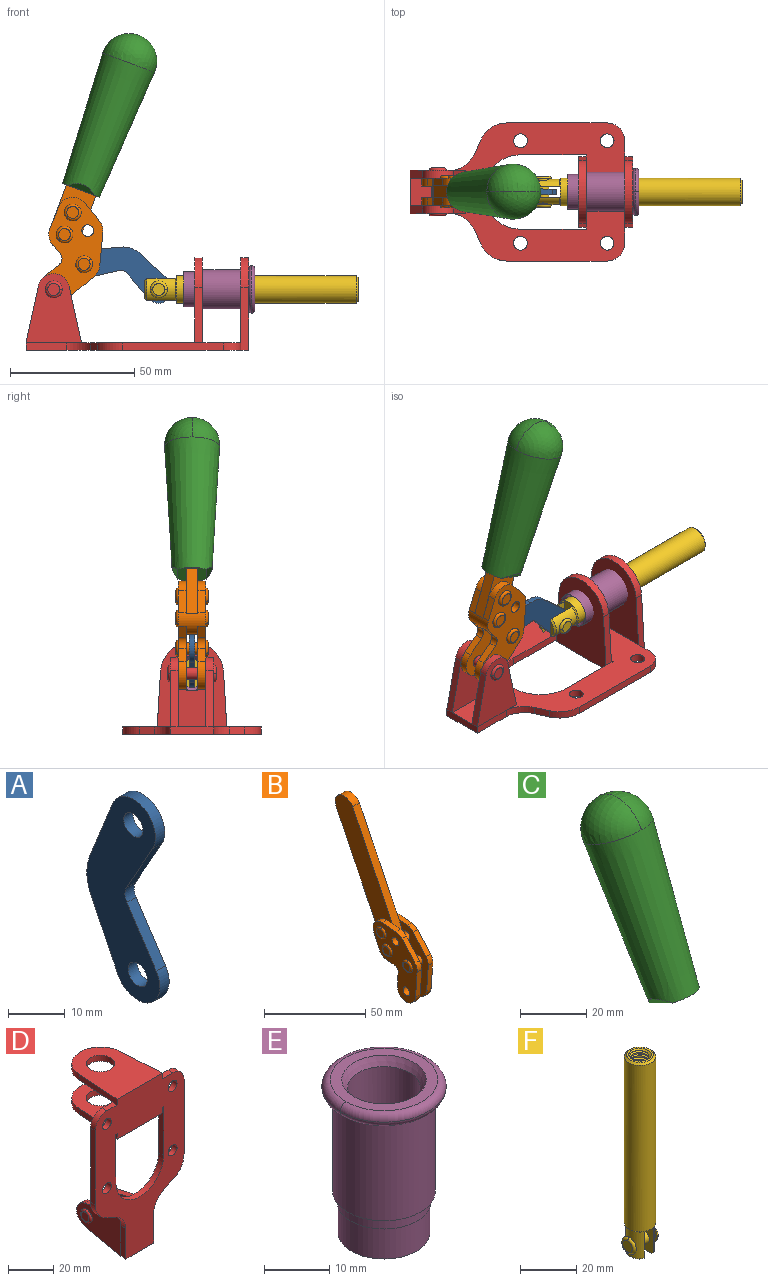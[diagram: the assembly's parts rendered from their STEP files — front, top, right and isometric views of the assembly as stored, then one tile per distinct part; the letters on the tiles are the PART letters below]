
ASSEMBLY  parts=6 mates=6
PART A: 12 faces, bbox 2.3x18.2x42.8 mm
  f0: cylinder r=2.4mm len=4.8mm, axis (1,0,0), area 34.9mm2, adj f4,f11
  f1: cylinder r=10.41mm len=8.47mm, axis (1,0,0), area 20.2mm2, adj f4,f9,f10,f11
  f2: cylinder r=3.05mm len=3.16mm, axis (1,0,0), area 7.7mm2, adj f4,f6,f7,f11
  f3: cylinder r=2.4mm len=4.8mm, axis (1,0,0), area 34.9mm2, adj f4,f11
  f4: plane 42.81x18.23mm, normal (-1,0,0), area 414.1mm2, adj f0,f1,f2,f3,f5,f6,f7,f8
  f5: cylinder r=5.54mm len=10.67mm, axis (1,0,0), area 41.8mm2, adj f4,f6,f10,f11
  f6: plane 11.66x6.53mm, normal (0,-0.87,-0.49), area 30.9mm2, adj f2,f4,f5,f11
  f7: plane 11.17x7.33mm, normal (0,-0.84,0.55), area 30.9mm2, adj f2,f4,f8,f11
  f8: cylinder r=5.54mm len=10.51mm, axis (1,0,0), area 41.8mm2, adj f4,f7,f9,f11
  f9: plane 13.67x6.67mm, normal (0,0.9,-0.44), area 35.1mm2, adj f1,f4,f8,f11
  f10: plane 14.1x5.7mm, normal (0,0.93,0.37), area 35.1mm2, adj f1,f4,f5,f11
  f11: plane 42.81x18.23mm, normal (1,0,0), area 414.1mm2, adj f0,f1,f2,f3,f5,f6,f7,f8
PART B: 59 faces, bbox 12.9x60.2x99.6 mm
  f0: torus R=2.39mm, axis (-1,0,0), area 14.9mm2, adj f20,f43,f51
  f1: torus R=2.39mm, axis (-1,0,0), area 14.9mm2, adj f19,f42,f51
  f2: torus R=2.39mm, axis (-1,0,0), area 14.9mm2, adj f18,f35,f51
  f3: torus R=2.39mm, axis (-1,0,0), area 14.9mm2, adj f14,f17,f23
  f4: torus R=2.39mm, axis (-1,0,0), area 14.9mm2, adj f13,f16,f23
  f5: torus R=2.39mm, axis (-1,0,0), area 14.9mm2, adj f12,f15,f23
  f6: cylinder r=2.39mm len=4.78mm, axis (1,0,0), area 46.5mm2, adj f48,f50,f51
  f7: cylinder r=2.39mm len=4.78mm, axis (1,0,0), area 46.5mm2, adj f50,f51
  f8: cylinder r=6.35mm len=12.68mm, axis (1,0,0), area 61.8mm2, adj f38,f39,f50,f51
  f9: cylinder r=2.39mm len=4.78mm, axis (-1,0,0), area 70.5mm2, adj f46,f50
  f10: cylinder r=2.39mm len=4.78mm, axis (-1,0,0), area 46.5mm2, adj f23,f45,f46
  f11: cylinder r=2.39mm len=4.78mm, axis (-1,0,0), area 46.5mm2, adj f23,f46
  f12: plane 4.78x4.78mm, normal (1,0,0), area 17.9mm2, adj f5,f15
  f13: plane 4.78x4.78mm, normal (1,0,0), area 17.9mm2, adj f4,f16
  f14: plane 4.78x4.78mm, normal (1,0,0), area 17.9mm2, adj f3,f17
  f15: torus R=2.39mm, axis (-1,0,0), area 14.9mm2, adj f5,f12,f23
  f16: torus R=2.39mm, axis (-1,0,0), area 14.9mm2, adj f4,f13,f23
  f17: torus R=2.39mm, axis (-1,0,0), area 14.9mm2, adj f3,f14,f23
  f18: plane 4.78x4.78mm, normal (-1,0,0), area 17.9mm2, adj f2,f35
  f19: plane 4.78x4.78mm, normal (-1,0,0), area 17.9mm2, adj f1,f42
  f20: plane 4.78x4.78mm, normal (-1,0,0), area 17.9mm2, adj f0,f43
  f21: plane 2.26x0.2mm, normal (1,0,0), area 0.2mm2, adj f31,f44
  f22: plane 2.26x0.2mm, normal (-1,0,0), area 0.2mm2, adj f41,f44
  f23: plane 39.37x30.77mm, normal (1,0,0), area 565.5mm2, adj f3,f4,f5,f10,f11,f15,f16,f17
  f24: cylinder r=6.1mm len=4.15mm, axis (-1,0,0), area 14.7mm2, adj f23,f25,f32,f46
  f25: plane 10.25x9.01mm, normal (0,-0.75,0.66), area 42.3mm2, adj f23,f24,f26,f46
  f26: cylinder r=6.35mm len=4.64mm, axis (-1,0,0), area 15.6mm2, adj f23,f25,f27,f46
  f27: plane 15.84x3.1mm, normal (0,-1,-0.07), area 49.2mm2, adj f23,f26,f28,f46
  f28: cylinder r=6.35mm len=12.68mm, axis (-1,0,0), area 61.8mm2, adj f23,f27,f29,f46
  f29: plane 8.11x3.1mm, normal (0,1,0.07), area 25.2mm2, adj f23,f28,f30,f46
  f30: cylinder r=3.05mm len=3.25mm, axis (-1,0,0), area 14.8mm2, adj f23,f29,f31,f46
  f31: plane 5.99x3.1mm, normal (0,0.07,-1), area 18.6mm2, adj f21,f23,f30,f44,f46
  f32: plane 9.5x3.1mm, normal (0,-0.07,1), area 29.5mm2, adj f23,f24,f33,f46,f47
  f33: cylinder r=6.1mm len=8.63mm, axis (-1,0,0), area 39.1mm2, adj f23,f32,f34,f47
  f34: plane 8.65x3.96mm, normal (0,0.91,-0.42), area 29.5mm2, adj f23,f33,f44,f47
  f35: torus R=2.39mm, axis (-1,0,0), area 14.9mm2, adj f2,f18,f51
  f36: plane 10.25x9.01mm, normal (0,-0.75,0.66), area 42.3mm2, adj f37,f49,f50,f51
  f37: cylinder r=6.35mm len=4.64mm, axis (1,0,0), area 15.6mm2, adj f36,f38,f50,f51
  f38: plane 15.84x3.1mm, normal (0,-1,-0.07), area 49.2mm2, adj f8,f37,f50,f51
  f39: plane 8.11x3.1mm, normal (0,1,0.07), area 25.2mm2, adj f8,f40,f50,f51
  f40: cylinder r=3.05mm len=3.25mm, axis (1,0,0), area 14.8mm2, adj f39,f41,f50,f51
  f41: plane 5.99x3.1mm, normal (0,0.07,-1), area 18.6mm2, adj f22,f40,f44,f50,f51
  f42: torus R=2.39mm, axis (-1,0,0), area 14.9mm2, adj f1,f19,f51
  f43: torus R=2.39mm, axis (-1,0,0), area 14.9mm2, adj f0,f20,f51
  f44: cylinder r=6.35mm len=12.12mm, axis (-1,0,0), area 128.9mm2, adj f21,f22,f23,f31,f34,f41,f46,f47
  f45: plane 2.65x1.35mm, normal (1,0,0), area 1mm2, adj f10,f55
  f46: plane 39.08x20.42mm, normal (-1,0,0), area 412.5mm2, adj f9,f10,f11,f24,f25,f26,f27,f28
  f47: plane 77.62x39.82mm, normal (1,0,0), area 850mm2, adj f32,f33,f34,f44,f53,f54,f55
  f48: plane 2.65x1.35mm, normal (-1,0,0), area 1mm2, adj f6,f55
  f49: cylinder r=6.1mm len=4.15mm, axis (1,0,0), area 14.7mm2, adj f36,f50,f51,f56
  f50: plane 39.08x20.42mm, normal (1,0,0), area 412.5mm2, adj f6,f7,f8,f9,f36,f37,f38,f39
  f51: plane 39.37x30.77mm, normal (-1,0,0), area 565.5mm2, adj f0,f1,f2,f6,f7,f8,f35,f36
  f52: plane 8.65x3.96mm, normal (0,0.91,-0.42), area 29.5mm2, adj f44,f51,f57,f58
  f53: plane 68.49x33.4mm, normal (0,0.9,-0.44), area 358.1mm2, adj f44,f47,f54,f58
  f54: cylinder r=6.35mm len=12.06mm, axis (1,0,0), area 93.7mm2, adj f47,f53,f55,f58
  f55: plane 68.49x33.4mm, normal (0,-0.9,0.44), area 358.1mm2, adj f44,f45,f46,f47,f48,f50,f54,f58
  f56: plane 9.5x3.1mm, normal (0,-0.07,1), area 29.5mm2, adj f49,f50,f51,f57,f58
  f57: cylinder r=6.1mm len=8.63mm, axis (1,0,0), area 39.1mm2, adj f51,f52,f56,f58
  f58: plane 77.62x39.82mm, normal (-1,0,0), area 850mm2, adj f44,f52,f53,f54,f55,f56,f57
PART C: 11 faces, bbox 22.3x42.6x64.5 mm
  f0: sphere r=11.13mm, area 411.4mm2, adj f1,f8
  f1: cone r=11.11mm half-angle=3.3deg, axis (0,0.44,0.9), area 3251.8mm2, adj f0,f7,f8,f9,f10
  f2: cylinder r=6.16mm len=11.7mm, axis (1,0,0), area 89.5mm2, adj f3,f4,f5,f6
  f3: plane 60.23x36.75mm, normal (-1,0,0), area 763.6mm2, adj f2,f4,f6,f10
  f4: plane 51.37x25.05mm, normal (0,0.9,-0.44), area 264.2mm2, adj f2,f3,f5,f10
  f5: plane 60.23x36.75mm, normal (1,0,0), area 763.6mm2, adj f2,f4,f6,f10
  f6: plane 51.37x25.05mm, normal (0,-0.9,0.44), area 264.2mm2, adj f2,f3,f5,f10
  f7: plane 9.95x5.95mm, normal (0.71,-0.31,-0.64), area 25.8mm2, adj f1,f10
  f8: sphere r=11.13mm, area 411.4mm2, adj f0,f1
  f9: plane 9.95x5.95mm, normal (-0.71,-0.31,-0.64), area 25.8mm2, adj f1,f10
  f10: plane 14.27x11.38mm, normal (0,-0.44,-0.9), area 106.7mm2, adj f1,f3,f4,f5,f6,f7,f9
PART D: 55 faces, bbox 55.7x37.4x89.8 mm
  f0: torus R=2.41mm, axis (-1,0,0), area 15mm2, adj f11,f15,f25
  f1: torus R=2.41mm, axis (-1,0,0), area 15mm2, adj f10,f12,f22
  f2: cylinder r=2.78mm len=5.56mm, axis (0,-1,0), area 54.2mm2, adj f30,f54
  f3: cylinder r=14.99mm len=29.97mm, axis (0,-1,0), area 145.9mm2, adj f30,f49,f53,f54
  f4: cylinder r=2.78mm len=5.56mm, axis (0,-1,0), area 54.2mm2, adj f30,f54
  f5: cylinder r=2.78mm len=5.56mm, axis (0,-1,0), area 54.2mm2, adj f30,f54
  f6: cylinder r=2.78mm len=5.56mm, axis (0,-1,0), area 54.2mm2, adj f30,f54
  f7: cylinder r=6.35mm len=12.7mm, axis (0,0,1), area 123.6mm2, adj f27,f51
  f8: cylinder r=6.35mm len=12.7mm, axis (0,0,-1), area 124.7mm2, adj f21,f35
  f9: cylinder r=2.41mm len=11.18mm, axis (-1,0,0), area 169.4mm2, adj f16,f19
  f10: plane 4.83x4.83mm, normal (1,0,0), area 18.3mm2, adj f1,f12
  f11: plane 4.83x4.83mm, normal (-1,0,0), area 18.3mm2, adj f0,f15
  f12: torus R=2.41mm, axis (-1,0,0), area 15mm2, adj f1,f10,f22
  f13: cylinder r=6.35mm len=12.41mm, axis (1,0,0), area 53.4mm2, adj f18,f19,f22,f23
  f14: cylinder r=6.35mm len=12.41mm, axis (-1,0,0), area 53.4mm2, adj f16,f17,f24,f25
  f15: torus R=2.41mm, axis (-1,0,0), area 15mm2, adj f0,f11,f25
  f16: plane 27.86x22.35mm, normal (1,0,0), area 425.4mm2, adj f9,f14,f17,f24,f30
  f17: plane 22.86x4.97mm, normal (0,0.21,0.98), area 72.5mm2, adj f14,f16,f25,f30
  f18: plane 22.86x4.97mm, normal (0,0.21,0.98), area 72.5mm2, adj f13,f19,f22,f30
  f19: plane 27.86x22.35mm, normal (-1,0,0), area 425.4mm2, adj f9,f13,f18,f23,f30
  f20: cylinder r=12.7mm len=25.35mm, axis (0,0,-1), area 119.8mm2, adj f21,f34,f35,f36
  f21: plane 34.21x28.07mm, normal (0,0,-1), area 702.4mm2, adj f8,f20,f30,f34,f36
  f22: plane 27.96x22.45mm, normal (1,0,0), area 407.2mm2, adj f1,f12,f13,f18,f23,f30,f42,f43
  f23: plane 22.86x4.97mm, normal (0,0.21,-0.98), area 72.5mm2, adj f13,f19,f22,f44
  f24: plane 22.86x4.97mm, normal (0,0.21,-0.98), area 72.5mm2, adj f14,f16,f25,f44
  f25: plane 27.86x22.35mm, normal (-1,0,0), area 407.1mm2, adj f0,f14,f15,f17,f24,f30,f45,f46
  f26: plane 3.1x0.95mm, normal (0,0,-1), area 2.7mm2, adj f30,f49,f50,f54
  f27: plane 34.21x28.07mm, normal (0,0,1), area 702.4mm2, adj f7,f28,f30,f50,f52
  f28: cylinder r=12.7mm len=25.35mm, axis (0,0,1), area 118.8mm2, adj f27,f50,f51,f52
  f29: plane 3.1x0.95mm, normal (0,0,-1), area 2.7mm2, adj f30,f52,f53,f54
  f30: plane 86.54x55.63mm, normal (0,1,0), area 2362.9mm2, adj f2,f3,f4,f5,f6,f16,f17,f18
  f31: plane 40.56x3.1mm, normal (-1,0,0), area 125.7mm2, adj f30,f32,f48,f54
  f32: cylinder r=7.11mm len=7.11mm, axis (0,-1,0), area 34.6mm2, adj f30,f31,f33,f54
  f33: plane 6.67x3.1mm, normal (0,0,1), area 20.4mm2, adj f30,f32,f34,f54
  f34: plane 25.39x3.13mm, normal (-1,0.06,0), area 79.5mm2, adj f20,f21,f33,f35,f54
  f35: plane 37.31x28.45mm, normal (0,0,1), area 789.9mm2, adj f8,f20,f34,f36,f54
  f36: plane 25.39x3.13mm, normal (1,0.06,0), area 79.5mm2, adj f20,f21,f35,f37,f54
  f37: plane 6.67x3.1mm, normal (0,0,1), area 20.4mm2, adj f30,f36,f38,f54
  f38: cylinder r=7.11mm len=7.11mm, axis (0,-1,0), area 34.6mm2, adj f30,f37,f39,f54
  f39: plane 40.56x3.1mm, normal (1,0,0), area 125.7mm2, adj f30,f38,f40,f54
  f40: cylinder r=11.18mm len=10.16mm, axis (0,-1,0), area 39.5mm2, adj f30,f39,f41,f54
  f41: plane 6.09x3.1mm, normal (0.42,0,-0.91), area 20.8mm2, adj f30,f40,f42,f54
  f42: cylinder r=11.18mm len=9.41mm, axis (0,-1,0), area 37.2mm2, adj f22,f30,f41,f43,f54
  f43: plane 16.5x3.1mm, normal (1,0,0), area 51.1mm2, adj f22,f42,f44,f54
  f44: plane 17.37x3.1mm, normal (0,0,-1), area 53.8mm2, adj f23,f24,f30,f43,f45,f54
  f45: plane 16.5x3.1mm, normal (-1,0,0), area 51.1mm2, adj f25,f44,f46,f54
  f46: cylinder r=11.18mm len=9.41mm, axis (0,-1,0), area 37.2mm2, adj f25,f30,f45,f47,f54
  f47: plane 6.09x3.1mm, normal (-0.42,0,-0.91), area 20.8mm2, adj f30,f46,f48,f54
  f48: cylinder r=11.18mm len=10.16mm, axis (0,-1,0), area 39.5mm2, adj f30,f31,f47,f54
  f49: plane 26.54x3.1mm, normal (-1,0,0), area 82.3mm2, adj f3,f26,f30,f54
  f50: plane 25.39x3.1mm, normal (1,0.06,0), area 78.8mm2, adj f26,f27,f28,f51,f54
  f51: plane 37.31x28.45mm, normal (0,0,-1), area 789.9mm2, adj f7,f28,f50,f52,f54
  f52: plane 25.39x3.1mm, normal (-1,0.06,0), area 78.8mm2, adj f27,f28,f29,f51,f54
  f53: plane 26.54x3.1mm, normal (1,0,0), area 82.3mm2, adj f3,f29,f30,f54
  f54: plane 89.66x55.63mm, normal (0,-1,0), area 2678.5mm2, adj f2,f3,f4,f5,f6,f26,f29,f31
PART E: 15 faces, bbox 20.6x20.6x28.7 mm
  f0: torus R=8.26mm, axis (0,0,1), area 56.8mm2, adj f1,f10,f12
  f1: torus R=8.26mm, axis (0,0,1), area 56.8mm2, adj f0,f6,f13
  f2: cylinder r=5.59mm len=25.91mm, axis (0,0,1), area 909.6mm2, adj f3,f4
  f3: cone r=6.86mm half-angle=45deg, axis (0,0,-1), area 70.2mm2, adj f2,f14
  f4: cone r=6.47mm half-angle=30deg, axis (0,0,1), area 66.7mm2, adj f2,f13
  f5: cylinder r=7.04mm len=14.07mm, axis (0,0,1), area 252.6mm2, adj f11,f14
  f6: torus R=8.26mm, axis (0,0,1), area 56.8mm2, adj f1,f12,f13
  f7: cylinder r=7.16mm len=14.33mm, axis (0,0,1), area 91.5mm2, adj f9,f11
  f8: cylinder r=7.86mm len=18.42mm, axis (0,0,1), area 909.6mm2, adj f9,f10
  f9: plane 15.72x15.72mm, normal (0,0,-1), area 33mm2, adj f7,f8
  f10: plane 16.51x16.51mm, normal (0,0,-1), area 19.9mm2, adj f0,f8,f12
  f11: plane 14.33x14.33mm, normal (0,0,-1), area 5.7mm2, adj f5,f7
  f12: torus R=8.26mm, axis (0,0,1), area 56.8mm2, adj f0,f6,f10
  f13: plane 16.51x16.51mm, normal (0,0,1), area 82.7mm2, adj f1,f4,f6
  f14: plane 14.07x14.07mm, normal (0,0,-1), area 7.8mm2, adj f3,f5
PART F: 48 faces, bbox 12.6x11.1x86.1 mm
  f0: torus R=2.41mm, axis (-1,0,0), area 15mm2, adj f30,f32,f34
  f1: torus R=2.41mm, axis (-1,0,0), area 15mm2, adj f29,f31,f33
  f2: cylinder r=5.54mm len=72.39mm, axis (0,0,1), area 2518.5mm2, adj f3,f4,f42,f43
  f3: cone r=5.54mm half-angle=45deg, axis (0,0,1), area 7.6mm2, adj f2,f5,f41
  f4: cone r=5.54mm half-angle=45deg, axis (0,0,-1), area 34.9mm2, adj f2,f39
  f5: cylinder r=5.08mm len=11.48mm, axis (0,0,1), area 108.3mm2, adj f3,f7,f8,f41
  f6: cylinder r=2.41mm len=4.83mm, axis (-1,0,0), area 71.2mm2, adj f40,f41
  f7: cylinder r=2.41mm len=4.83mm, axis (-1,0,0), area 7.6mm2, adj f5,f34
  f8: cone r=5.08mm half-angle=45deg, axis (0,0,1), area 10.6mm2, adj f5,f37,f41
  f9: cone r=3.98mm half-angle=45deg, axis (0,0,1), area 17.6mm2, adj f27,f39,f45,f46,f47
  f10: cylinder r=2.41mm len=4.83mm, axis (-1,0,0), area 7.6mm2, adj f33,f38
  f11: cylinder r=3.2mm len=6.4mm, axis (0,0,1), area 78.4mm2, adj f12,f28,f44,f45,f47
  f12: cylinder r=3.2mm len=6.4mm, axis (0,0,1), area 10.5mm2, adj f11,f13,f45,f47
  f13: cylinder r=3.2mm len=6.4mm, axis (0,0,1), area 10.5mm2, adj f12,f14,f45,f47
  f14: cylinder r=3.2mm len=6.4mm, axis (0,0,1), area 10.5mm2, adj f13,f15,f45,f47
  f15: cylinder r=3.2mm len=6.4mm, axis (0,0,1), area 10.5mm2, adj f14,f16,f45,f47
  f16: cylinder r=3.2mm len=6.4mm, axis (0,0,1), area 10.5mm2, adj f15,f17,f45,f47
  f17: cylinder r=3.2mm len=6.4mm, axis (0,0,1), area 10.5mm2, adj f16,f18,f45,f47
  f18: cylinder r=3.2mm len=6.4mm, axis (0,0,1), area 10.5mm2, adj f17,f19,f45,f47
  f19: cylinder r=3.2mm len=6.4mm, axis (0,0,1), area 10.5mm2, adj f18,f20,f45,f47
  f20: cylinder r=3.2mm len=6.4mm, axis (0,0,1), area 10.5mm2, adj f19,f21,f45,f47
  f21: cylinder r=3.2mm len=6.4mm, axis (0,0,1), area 10.5mm2, adj f20,f22,f45,f47
  f22: cylinder r=3.2mm len=6.4mm, axis (0,0,1), area 10.5mm2, adj f21,f23,f45,f47
  f23: cylinder r=3.2mm len=6.4mm, axis (0,0,1), area 10.5mm2, adj f22,f24,f45,f47
  f24: cylinder r=3.2mm len=6.4mm, axis (0,0,1), area 10.5mm2, adj f23,f25,f45,f47
  f25: cylinder r=3.2mm len=6.4mm, axis (0,0,1), area 10.5mm2, adj f24,f26,f45,f47
  f26: cylinder r=3.2mm len=6.4mm, axis (0,0,1), area 10.5mm2, adj f25,f27,f45,f47
  f27: cylinder r=3.2mm len=6.4mm, axis (0,0,1), area 7.4mm2, adj f9,f26,f45,f47
  f28: cone r=3.2mm half-angle=60deg, axis (0,0,1), area 37.2mm2, adj f11
  f29: plane 4.83x4.83mm, normal (-1,0,0), area 18.3mm2, adj f1,f31
  f30: plane 4.83x4.83mm, normal (1,0,0), area 18.3mm2, adj f0,f32
  f31: torus R=2.41mm, axis (-1,0,0), area 15mm2, adj f1,f29,f33
  f32: torus R=2.41mm, axis (-1,0,0), area 15mm2, adj f0,f30,f34
  f33: plane 6.83x6.83mm, normal (1,0,0), area 18.3mm2, adj f1,f10,f31
  f34: plane 6.83x6.83mm, normal (-1,0,0), area 18.3mm2, adj f0,f7,f32
  f35: cone r=5.08mm half-angle=45deg, axis (0,0,1), area 10.6mm2, adj f36,f38,f40
  f36: plane 7.25x1.97mm, normal (0,0,-1), area 10mm2, adj f35,f40
  f37: plane 7.25x1.97mm, normal (0,0,-1), area 10mm2, adj f8,f41
  f38: cylinder r=5.08mm len=11.48mm, axis (0,0,1), area 108.3mm2, adj f10,f35,f40,f42
  f39: plane 9.55x9.55mm, normal (0,0,1), area 22mm2, adj f4,f9
  f40: plane 12.76x10.09mm, normal (1,0,0), area 95.7mm2, adj f6,f35,f36,f38,f42,f43
  f41: plane 12.76x10.09mm, normal (-1,0,0), area 95.7mm2, adj f3,f5,f6,f8,f37,f43
  f42: cone r=5.54mm half-angle=45deg, axis (0,0,1), area 7.6mm2, adj f2,f38,f40
  f43: plane 11.07x4.7mm, normal (0,0,-1), area 50.4mm2, adj f2,f40,f41
  f44: plane 0.89x0.62mm, normal (-1,0,0), area 0.3mm2, adj f11,f45,f46,f47
  f45: bspline ~24.8x7.63mm, area 266.6mm2, adj f9,f11,f12,f13,f14,f15,f16,f17
  f46: bspline ~24.87x7.63mm, area 73.6mm2, adj f9,f44,f45,f47
  f47: bspline ~24.98x7.63mm, area 272.5mm2, adj f9,f11,f12,f13,f14,f15,f16,f17
PLACE A rot(axis=(0.51,-0.51,-0.69),110.9deg) t=(-21.18,0,6.72)mm
PLACE B rot(axis=(0.37,0.37,0.85),98.9deg) t=(-1.01,0,28.88)mm
PLACE C rot(axis=(0.37,0.37,0.85),98.9deg) t=(-1.01,-0.04,28.88)mm
PLACE D rot(axis=(0.58,0.58,0.58),120deg) t=(-9.14,0,0)mm fixed
PLACE E rot(axis=(0.71,0,0.71),180deg) t=(-9.14,24.61,24.61)mm
PLACE F rot(axis=(-0.58,0.58,-0.58),120deg) t=(-14.37,0,49.23)mm
MATE revolute A.f5 <-> B.f4  axis (0,-1,0) through (-28.99,0,34.72)mm
MATE slider F.f2 <-> E.f2  axis (1,0,0) through (44.41,0,24.61)mm
MATE fastened E.f0 <-> D.f7  axis (-1,0,0) through (37.25,0,24.61)mm
MATE revolute B.f7 <-> D.f0  axis (0,-1,0) through (-41.23,0,24.61)mm
MATE revolute A.f3 <-> F.f6  axis (0,-1,0) through (1.11,0,24.61)mm
MATE fastened C.f2 <-> B.f54  axis (0,1,0) through (-10.26,-2.35,118.11)mm
